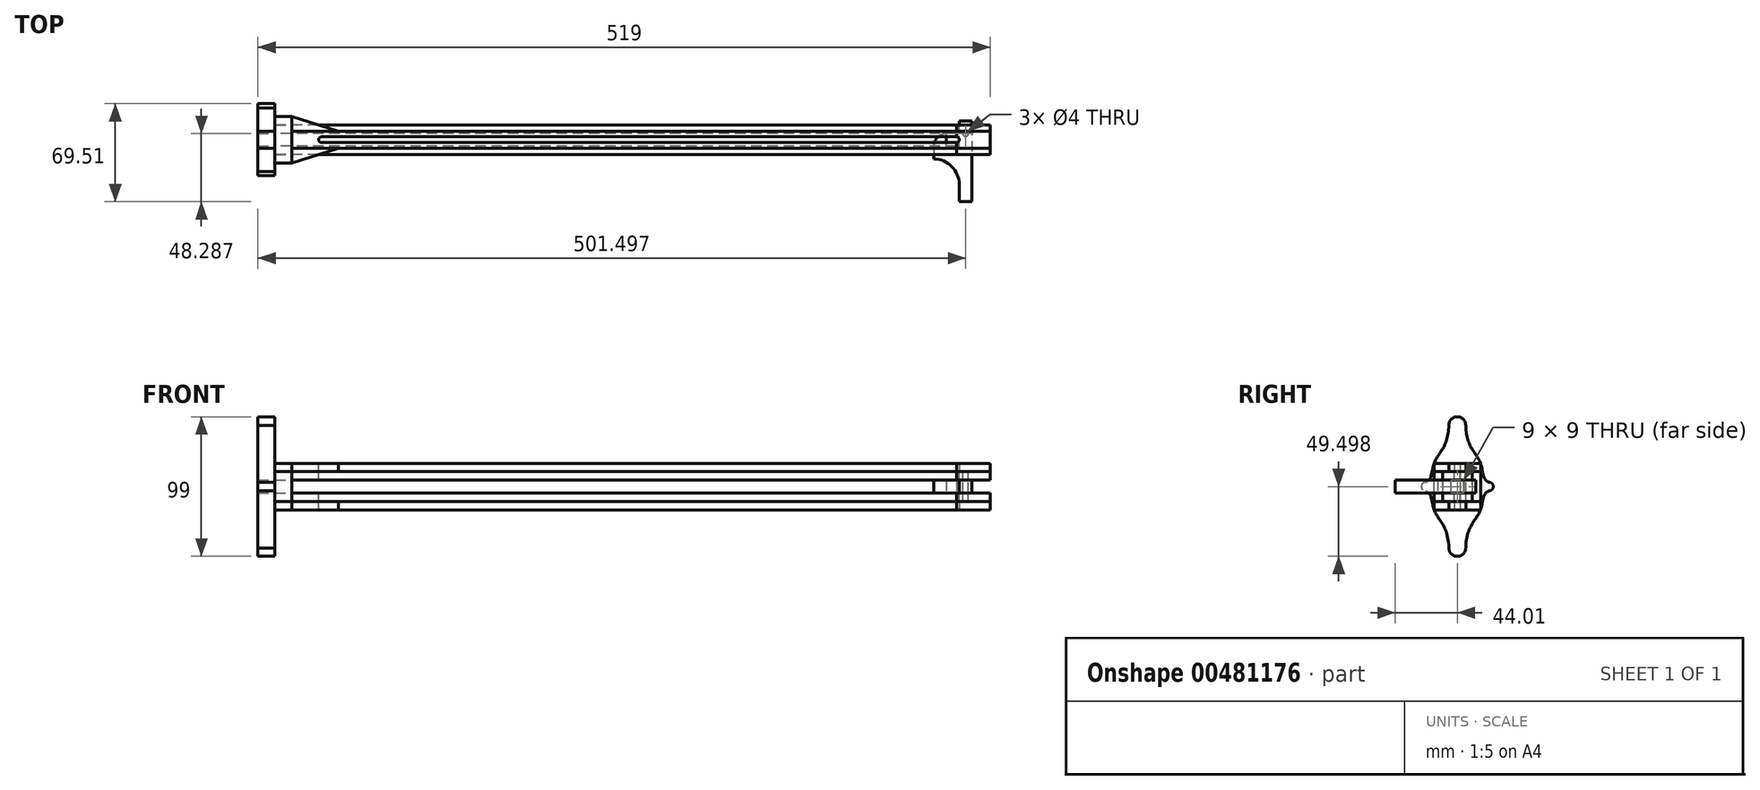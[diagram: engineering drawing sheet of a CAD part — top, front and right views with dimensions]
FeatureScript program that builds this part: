
annotation { "Feature Type Name" : "Feature", "Feature Type Description" : "" }
export const myFeature = defineFeature(function(context is Context, id is Id, definition is map)
    precondition{}
    {
        {
            var Q0;
            Q0=qCreatedBy(makeId("Front.planeOp"),FACE);
            var sketch = newSketch(context, id + "F0", { "sketchPlane" : qUnion([Q0])});
            skLineSegment(sketch, "E0", {"start": v(-257.14, -33.26) * mm, "end": v(225.86, -33.26) * mm});
            skLineSegment(sketch, "E1", {"start": v(-257.14, -42.26) * mm, "end": v(225.86, -42.26) * mm});
            skLineSegment(sketch, "E2", {"start": v(-257.14, -27.26) * mm, "end": v(-257.14, -33.26) * mm});
            skLineSegment(sketch, "E3", {"start": v(-257.14, -27.26) * mm, "end": v(-257.14, -21.26) * mm});
            skLineSegment(sketch, "E4", {"start": v(225.86, -33.26) * mm, "end": v(225.86, -27.26) * mm});
            skLineSegment(sketch, "E5", {"start": v(225.86, -27.26) * mm, "end": v(-257.14, -27.26) * mm});
            skLineSegment(sketch, "E6", {"start": v(225.86, -27.26) * mm, "end": v(225.86, -21.26) * mm});
            skLineSegment(sketch, "E7", {"start": v(225.86, -21.26) * mm, "end": v(-257.14, -21.26) * mm});
            skLineSegment(sketch, "E8", {"start": v(225.86, -42.26) * mm, "end": v(225.86, -48.26) * mm});
            skLineSegment(sketch, "E9", {"start": v(-257.14, -42.26) * mm, "end": v(-257.14, -48.26) * mm});
            skLineSegment(sketch, "E10", {"start": v(-257.14, -48.26) * mm, "end": v(225.86, -48.26) * mm});
            skLineSegment(sketch, "E11", {"start": v(-257.14, -48.26) * mm, "end": v(-257.14, -54.26) * mm});
            skLineSegment(sketch, "E12", {"start": v(225.86, -48.26) * mm, "end": v(225.86, -54.26) * mm});
            skLineSegment(sketch, "E13", {"start": v(225.86, -54.26) * mm, "end": v(-257.14, -54.26) * mm});
            skLineSegment(sketch, "E14", {"start": v(-257.14, -21.26) * mm, "end": v(-245.14, -21.26) * mm});
            skLineSegment(sketch, "E15", {"start": v(-245.14, -21.26) * mm, "end": v(-245.14, -54.26) * mm});
            skLineSegment(sketch, "E16", {"start": v(-245.14, -54.26) * mm, "end": v(-257.14, -54.26) * mm});
            skSolve(sketch);
        }
        {
            var Q0;
            Q0=makeQuery(id+"F0.imprint","IMPRINT",FACE,{"disambiguationData":[TD([[makeQuery(id+"F0.imprint","IMPRINT",EDGE,{"derivedFrom":sQuery(id+"F0.wireOp",EDGE,"E0")}),1.0]])]});
            var Q1;
            Q1=makeQuery(id+"F0.imprint","IMPRINT",FACE,{"disambiguationData":[TD([[makeQuery(id+"F0.imprint","IMPRINT",EDGE,{"derivedFrom":sQuery(id+"F0.wireOp",EDGE,"E1")}),-1.0]])]});
            extrude(context, id + "F1", {"entities" : qUnion([Q0, Q1]), "depth" : 10.5 * mm, "offsetDistance" : 25 * mm, "hasSecondDirection" : true, "secondDirectionOppositeDirection" : true, "secondDirectionDepth" : 10.5 * mm});
        }
        {
            var Q0;
            {var subQ0=sQuery(id+"F0.wireOp",EDGE,"E3");Q0=makeQuery(id+"F0.imprint","IMPRINT",FACE,{"disambiguationData":[TD([[makeQuery(id+"F0.imprint","IMPRINT",EDGE,{"derivedFrom":subQ0}),-1.0]])]});}
            var Q1;
            {var subQ0=sQuery(id+"F0.wireOp",EDGE,"E11");Q1=makeQuery(id+"F0.imprint","IMPRINT",FACE,{"disambiguationData":[TD([[makeQuery(id+"F0.imprint","IMPRINT",EDGE,{"derivedFrom":subQ0}),1.0]])]});}
            extrude(context, id + "F2", {"entities" : qUnion([Q0, Q1]), "depth" : (16.5) * mm, "offsetDistance" : 25 * mm, "hasSecondDirection" : true, "secondDirectionOppositeDirection" : true, "secondDirectionDepth" : 16.5 * mm});
        }
        {
            var Q0;
            {var subQ0=sQuery(id+"F0.wireOp",EDGE,"E12");Q0=makeQuery(id+"F0.imprint","IMPRINT",FACE,{"disambiguationData":[TD([[makeQuery(id+"F0.imprint","IMPRINT",EDGE,{"derivedFrom":subQ0}),-1.0]])]});}
            var Q1;
            {var subQ0=sQuery(id+"F0.wireOp",EDGE,"E6");Q1=makeQuery(id+"F0.imprint","IMPRINT",FACE,{"disambiguationData":[TD([[makeQuery(id+"F0.imprint","IMPRINT",EDGE,{"derivedFrom":subQ0}),1.0]])]});}
            extrude(context, id + "F3", {"entities" : qUnion([Q0, Q1]), "depth" : 6 * mm, "offsetDistance" : 25 * mm, "hasSecondDirection" : true, "secondDirectionOppositeDirection" : true, "secondDirectionDepth" : 6 * mm});
        }
        {
            var Q0;
            Q0=makeQuery(id+"F2.opExtrude","SWEPT_FACE",FACE,{"disambiguationData":[OSD([sQuery(id+"F0.wireOp",EDGE,"E5")])]});
            var sketch = newSketch(context, id + "F4", { "sketchPlane" : qUnion([Q0])});
            skLineSegment(sketch, "E17.bottom", {"start": v(-257.14, 16.5) * mm, "end": v(-245.14, 16.5) * mm});
            skLineSegment(sketch, "E17.top", {"start": v(-257.14, 10.5) * mm, "end": v(-245.14, 10.5) * mm});
            skLineSegment(sketch, "E17.left", {"start": v(-257.14, 16.5) * mm, "end": v(-257.14, 10.5) * mm});
            skLineSegment(sketch, "E17.right", {"start": v(-245.14, 16.5) * mm, "end": v(-245.14, 10.5) * mm});
            skLineSegment(sketch, "E18.bottom", {"start": v(-257.14, -16.5) * mm, "end": v(-245.14, -16.5) * mm});
            skLineSegment(sketch, "E18.top", {"start": v(-257.14, -10.5) * mm, "end": v(-245.14, -10.5) * mm});
            skLineSegment(sketch, "E18.left", {"start": v(-257.14, -16.5) * mm, "end": v(-257.14, -10.5) * mm});
            skLineSegment(sketch, "E18.right", {"start": v(-245.14, -16.5) * mm, "end": v(-245.14, -10.5) * mm});
            skSolve(sketch);
        }
        {
            var Q0;
            Q0 = qSketchRegion(id + "F4", true);
            extrude(context, id + "F5", {"entities" : qUnion([Q0]), "depth" : 21 * mm, "offsetDistance" : 25 * mm});
        }
        {
            var Q0;
            Q0=makeQuery(id+"F1.opExtrude","SWEPT_FACE",FACE,{"disambiguationData":[OSD([sQuery(id+"F0.wireOp",EDGE,"E2")])]});
            var sketch = newSketch(context, id + "F6", { "sketchPlane" : qUnion([Q0])});
            skLineSegment(sketch, "E19.bottom", {"start": v(10.5, -33.26) * mm, "end": v(4.5, -33.26) * mm});
            skLineSegment(sketch, "E19.top", {"start": v(10.5, -42.26) * mm, "end": v(4.5, -42.26) * mm});
            skLineSegment(sketch, "E19.left", {"start": v(10.5, -33.26) * mm, "end": v(10.5, -42.26) * mm});
            skLineSegment(sketch, "E19.right", {"start": v(4.5, -33.26) * mm, "end": v(4.5, -42.26) * mm});
            skLineSegment(sketch, "E20.bottom", {"start": v(-10.5, -33.26) * mm, "end": v(-4.5, -33.26) * mm});
            skLineSegment(sketch, "E20.top", {"start": v(-10.5, -42.26) * mm, "end": v(-4.5, -42.26) * mm});
            skLineSegment(sketch, "E20.left", {"start": v(-10.5, -33.26) * mm, "end": v(-10.5, -42.26) * mm});
            skLineSegment(sketch, "E20.right", {"start": v(-4.5, -33.26) * mm, "end": v(-4.5, -42.26) * mm});
            skSolve(sketch);
        }
        {
            var Q0;
            Q0 = qSketchRegion(id + "F6", true);
            extrude(context, id + "F7", {"entities" : qUnion([Q0]), "oppositeDirection" : true, "depth" : 483 * mm, "offsetDistance" : 25 * mm});
        }
        {
            var Q0;
            Q0=makeQuery(id+"F3.opExtrude","SWEPT_FACE",FACE,{"disambiguationData":[OSD([sQuery(id+"F0.wireOp",EDGE,"E7")])]});
            var sketch = newSketch(context, id + "F8", { "sketchPlane" : qUnion([Q0])});
            skLineSegment(sketch, "E21", {"start": v(-245.14, 6) * mm, "end": v(-245.14, 16.5) * mm});
            skLineSegment(sketch, "E22.MirrorCS", {"start": v(-245.14, -6) * mm, "end": v(-245.14, -16.5) * mm});
            skLineSegment(sketch, "E23", {"start": v(-212.14, -6) * mm, "end": v(-245.14, -16.5) * mm});
            skLineSegment(sketch, "E24", {"start": v(-212.14, 6) * mm, "end": v(-245.14, 16.5) * mm});
            skLineSegment(sketch, "E25", {"start": v(-212.14, -6) * mm, "end": v(-245.14, -6) * mm});
            skLineSegment(sketch, "E26", {"start": v(-245.14, 6) * mm, "end": v(-212.14, 6) * mm});
            skSolve(sketch);
        }
        {
            var Q0;
            Q0=makeQuery(id+"F3.opExtrude","SWEPT_FACE",FACE,{"disambiguationData":[OSD([sQuery(id+"F0.wireOp",EDGE,"E7")])]});
            var sketch = newSketch(context, id + "F9", { "sketchPlane" : qUnion([Q0])});
            skLineSegment(sketch, "E27", {"start": v(225.86, 0) * mm, "end": v(-224.14, 0) * mm});
            skSolve(sketch);
        }
        {
            var Q0;
            Q0 = qSketchRegion(id + "F8", true);
            extrude(context, id + "F10", {"entities" : qUnion([Q0]), "oppositeDirection" : true, "depth" : 6 * mm, "offsetDistance" : 25 * mm});
        }
        {
            var Q0;
            Q0=makeQuery(id+"F1.opExtrude","SWEPT_FACE",FACE,{"disambiguationData":[OSD([sQuery(id+"F0.wireOp",EDGE,"E10")])]});
            var sketch = newSketch(context, id + "F11", { "sketchPlane" : qUnion([Q0])});
            skLineSegment(sketch, "E28", {"start": v(-257.14, -10.5) * mm, "end": v(-245.14, -10.5) * mm});
            skLineSegment(sketch, "E29", {"start": v(-245.14, -10.5) * mm, "end": v(-245.14, -16.5) * mm});
            skLineSegment(sketch, "E30", {"start": v(-245.14, -10.5) * mm, "end": v(-245.14, -6) * mm});
            skLineSegment(sketch, "E31", {"start": v(-245.14, -6) * mm, "end": v(-212.14, -6) * mm});
            skLineSegment(sketch, "E32", {"start": v(-245.14, -16.5) * mm, "end": v(-212.14, -6) * mm});
            skLineSegment(sketch, "E33", {"start": v(-245.14, -6) * mm, "end": v(-245.14, 6) * mm});
            skLineSegment(sketch, "E34", {"start": v(-245.14, 0) * mm, "end": v(-224.95, 0) * mm});
            skLineSegment(sketch, "E35.MirrorCS", {"start": v(-245.14, 10.5) * mm, "end": v(-245.14, 16.5) * mm});
            skLineSegment(sketch, "E36.MirrorCS", {"start": v(-257.14, 10.5) * mm, "end": v(-245.14, 10.5) * mm});
            skLineSegment(sketch, "E37.MirrorCS", {"start": v(-245.14, 16.5) * mm, "end": v(-212.14, 6) * mm});
            skLineSegment(sketch, "E38.MirrorCS", {"start": v(-245.14, 6) * mm, "end": v(-212.14, 6) * mm});
            skLineSegment(sketch, "E39.MirrorCS", {"start": v(-245.14, 6) * mm, "end": v(-245.14, -6) * mm});
            skLineSegment(sketch, "E40.MirrorCS", {"start": v(-245.14, 10.5) * mm, "end": v(-245.14, 6) * mm});
            skSolve(sketch);
        }
        {
            var Q0;
            {var subQ0=sQuery(id+"F11.wireOp",EDGE,"E30");Q0=makeQuery(id+"F11.imprint","IMPRINT",FACE,{"disambiguationData":[TD([[makeQuery(id+"F11.imprint","IMPRINT",EDGE,{"derivedFrom":subQ0}),-1.0]])]});}
            var Q1;
            {var subQ0=sQuery(id+"F11.wireOp",EDGE,"E29");Q1=makeQuery(id+"F11.imprint","IMPRINT",FACE,{"disambiguationData":[TD([[makeQuery(id+"F11.imprint","IMPRINT",EDGE,{"derivedFrom":subQ0}),1.0]])]});}
            var Q2;
            {var subQ0=sQuery(id+"F11.wireOp",EDGE,"E35.MirrorCS");Q2=makeQuery(id+"F11.imprint","IMPRINT",FACE,{"disambiguationData":[TD([[makeQuery(id+"F11.imprint","IMPRINT",EDGE,{"derivedFrom":subQ0}),-1.0]])]});}
            var Q3;
            {var subQ0=sQuery(id+"F11.wireOp",EDGE,"E38.MirrorCS");Q3=makeQuery(id+"F11.imprint","IMPRINT",FACE,{"disambiguationData":[TD([[makeQuery(id+"F11.imprint","IMPRINT",EDGE,{"derivedFrom":subQ0}),1.0]])]});}
            extrude(context, id + "F12", {"entities" : qUnion([Q0, Q1, Q2, Q3]), "depth" : 6 * mm, "offsetDistance" : 25 * mm});
        }
        {
            var Q0;
            Q0=sQuery(id+"F9.wireOp",VERTEX,"E27.end");
            var Q1;
            Q1=sQuery(id+"F9.wireOp",VERTEX,"E27.start");
            var Q2;
            Q2=makeQuery(id+"F1.opExtrude","SWEPT_BODY",BODY,{"disambiguationData":[OSD([sQuery(id+"F0.wireOp",EDGE,"E0"),sQuery(id+"F0.wireOp",EDGE,"E2"),sQuery(id+"F0.wireOp",EDGE,"E4"),sQuery(id+"F0.wireOp",EDGE,"E5")])]});
            var Q3;
            Q3=makeQuery(id+"F1.opExtrude","SWEPT_BODY",BODY,{"disambiguationData":[OSD([sQuery(id+"F0.wireOp",EDGE,"E1"),sQuery(id+"F0.wireOp",EDGE,"E8"),sQuery(id+"F0.wireOp",EDGE,"E9"),sQuery(id+"F0.wireOp",EDGE,"E10")])]});
            var Q4;
            Q4=makeQuery(id+"F3.opExtrude","SWEPT_BODY",BODY,{"disambiguationData":[OSD([sQuery(id+"F0.wireOp",EDGE,"E5"),sQuery(id+"F0.wireOp",EDGE,"E6"),sQuery(id+"F0.wireOp",EDGE,"E7"),sQuery(id+"F0.wireOp",EDGE,"E15")])]});
            var Q5;
            Q5=makeQuery(id+"F3.opExtrude","SWEPT_BODY",BODY,{"disambiguationData":[OSD([sQuery(id+"F0.wireOp",EDGE,"E10"),sQuery(id+"F0.wireOp",EDGE,"E12"),sQuery(id+"F0.wireOp",EDGE,"E13"),sQuery(id+"F0.wireOp",EDGE,"E15")])]});
            hole(context, id + "F13", {"style" : HoleStyle.SIMPLE, "endStyle" : HoleEndStyle.THROUGH, "holeDiameter" : 4 * mm, "majorDiameter" : 5 * mm, "isTappedThrough" : true, "tappedDepth" : 12 * mm, "tapClearance" : 3, "locations" : qUnion([Q0, Q1]), "scope" : qUnion([Q2, Q3, Q4, Q5])});
        }
        {
            var Q0;
            Q0=makeQuery(id+"F3.opExtrude","SWEPT_FACE",FACE,{"disambiguationData":[OSD([sQuery(id+"F0.wireOp",EDGE,"E7")])]});
            var sketch = newSketch(context, id + "F14", { "sketchPlane" : qUnion([Q0])});
            skLineSegment(sketch, "E41.bottom", {"start": v(225.86, 2) * mm, "end": v(-224.14, 2) * mm});
            skLineSegment(sketch, "E41.top", {"start": v(225.86, -2) * mm, "end": v(-224.14, -2) * mm});
            skLineSegment(sketch, "E41.left", {"start": v(225.86, 2) * mm, "end": v(225.86, -2) * mm});
            skLineSegment(sketch, "E41.right", {"start": v(-224.14, 2) * mm, "end": v(-224.14, -2) * mm});
            skSolve(sketch);
        }
        {
            var Q0;
            Q0 = qSketchRegion(id + "F14", true);
            extrude(context, id + "F15", {"entities" : qUnion([Q0]), "operationType" : NewBodyOperationType.REMOVE, "oppositeDirection" : true, "depth" : 45 * mm, "offsetDistance" : 25 * mm});
        }
        {
            var Q0;
            {var subQ0=sQuery(id+"F0.wireOp",EDGE,"E5");var subQ1=sQuery(id+"F0.wireOp",EDGE,"E7");var subQ2=sQuery(id+"F0.wireOp",EDGE,"E6");Q0=makeQuery(id+"F13.hole-1.boolean.opBoolean","SPLIT",FACE,{"disambiguationData":[TD([makeQuery(id+"F3.opExtrude","CAP_FACE",FACE,{"disambiguationData":[OSD([subQ0,subQ2,subQ1,sQuery(id+"F0.wireOp",EDGE,"E15")])],"isStart":true})])],"derivedFrom":makeQuery(id+"F3.opExtrude","SWEPT_FACE",FACE,{"disambiguationData":[OSD([subQ2])]})});}
            var sketch = newSketch(context, id + "F16", { "sketchPlane" : qUnion([Q0])});
            skLineSegment(sketch, "E42", {"start": v(6, -21.26) * mm, "end": v(-6, -21.26) * mm});
            skLineSegment(sketch, "E43", {"start": v(6, -27.26) * mm, "end": v(-6, -27.26) * mm});
            skLineSegment(sketch, "E44", {"start": v(6, -21.26) * mm, "end": v(6, -27.26) * mm});
            skLineSegment(sketch, "E45", {"start": v(-6, -21.26) * mm, "end": v(-6, -27.26) * mm});
            skLineSegment(sketch, "E46", {"start": v(6, -54.26) * mm, "end": v(-6, -54.26) * mm});
            skLineSegment(sketch, "E47", {"start": v(-6, -54.26) * mm, "end": v(-6, -48.26) * mm});
            skLineSegment(sketch, "E48", {"start": v(-6, -48.26) * mm, "end": v(6, -48.26) * mm});
            skLineSegment(sketch, "E49", {"start": v(6, -48.26) * mm, "end": v(6, -54.26) * mm});
            skSolve(sketch);
        }
        {
            var Q0;
            Q0 = qSketchRegion(id + "F16", true);
            extrude(context, id + "F17", {"entities" : qUnion([Q0]), "depth" : 24 * mm, "offsetDistance" : 25 * mm});
        }
        {
            var Q0;
            Q0=makeQuery(id+"F1.opExtrude","SWEPT_FACE",FACE,{"disambiguationData":[OSD([sQuery(id+"F0.wireOp",EDGE,"E9")])]});
            var sketch = newSketch(context, id + "F18", { "sketchPlane" : qUnion([Q0])});
            skLineSegment(sketch, "E50", {"start": v(0, -54.26) * mm, "end": v(0, -87.26) * mm});
            skLineSegment(sketch, "E51", {"start": v(0, -21.26) * mm, "end": v(0, 11.74) * mm});
            skLineSegment(sketch, "E52", {"start": v(-16.5, -37.76) * mm, "end": v(-22.5, -37.76) * mm});
            skLineSegment(sketch, "E53", {"start": v(16.5, -37.76) * mm, "end": v(22.5, -37.76) * mm});
            skCircle(sketch, "E54", {"center": v(-22.5, -37.76) * mm, "radius": 3 * mm});
            skLineSegment(sketch, "E55", {"start": v(16.5, -37.76) * mm, "end": v(19.5, -37.76) * mm});
            skCircle(sketch, "E56", {"center": v(22.5, -37.76) * mm, "radius": 3 * mm});
            skLineSegment(sketch, "E57", {"start": v(-16.5, -37.76) * mm, "end": v(-16.5, -27.26) * mm});
            skLineSegment(sketch, "E58", {"start": v(16.5, -37.76) * mm, "end": v(16.5, -48.26) * mm});
            skLineSegment(sketch, "E59", {"start": v(16.5, -37.76) * mm, "end": v(16.5, -27.26) * mm});
            skLineSegment(sketch, "E60", {"start": v(0, -87.26) * mm, "end": v(0, -84.26) * mm});
            skLineSegment(sketch, "E61", {"start": v(0, 11.74) * mm, "end": v(0, 8.74) * mm});
            skLineSegment(sketch, "E62", {"start": v(0, -87.26) * mm, "end": v(0, -81.26) * mm});
            skCircle(sketch, "E63", {"center": v(0, -81.26) * mm, "radius": 6 * mm});
            skLineSegment(sketch, "E64", {"start": v(0, -21.26) * mm, "end": v(0, 5.74) * mm});
            skCircle(sketch, "E65", {"center": v(0, 5.74) * mm, "radius": 6 * mm});
            skLineSegment(sketch, "E66.bottom", {"start": v(-16.5, -54.26) * mm, "end": v(16.5, -54.26) * mm});
            skLineSegment(sketch, "E66.top", {"start": v(-16.5, -21.26) * mm, "end": v(16.5, -21.26) * mm});
            skLineSegment(sketch, "E66.left", {"start": v(-16.5, -54.26) * mm, "end": v(-16.5, -21.26) * mm});
            skLineSegment(sketch, "E66.right", {"start": v(16.5, -54.26) * mm, "end": v(16.5, -21.26) * mm});
            skLineSegment(sketch, "E67", {"start": v(-4.5, -37.76) * mm, "end": v(-4.5, -33.26) * mm});
            skLineSegment(sketch, "E68", {"start": v(4.5, -37.76) * mm, "end": v(4.5, -42.26) * mm});
            skLineSegment(sketch, "E69.bottom", {"start": v(4.5, -42.26) * mm, "end": v(-4.5, -42.26) * mm});
            skLineSegment(sketch, "E69.top", {"start": v(4.5, -33.26) * mm, "end": v(-4.5, -33.26) * mm});
            skLineSegment(sketch, "E69.left", {"start": v(4.5, -42.26) * mm, "end": v(4.5, -33.26) * mm});
            skLineSegment(sketch, "E69.right", {"start": v(-4.5, -42.26) * mm, "end": v(-4.5, -33.26) * mm});
            skFitSpline(sketch, "E70", {"points": [v(-22.5, -40.76) * mm, v(-16.5, -54.26) * mm, v(-6, -81.26) * mm], "startDerivative": vector(34.79, -10.64) * mm, "endDerivative": vector(1.67, -81.78) * mm});
            skFitSpline(sketch, "E71.MirrorCS", {"points": [v(-22.5, -34.76) * mm, v(-16.5, -21.26) * mm, v(-6, 5.74) * mm], "startDerivative": vector(34.79, 10.64) * mm, "endDerivative": vector(1.67, 81.78) * mm});
            skFitSpline(sketch, "E72.MirrorCS", {"points": [v(22.5, -34.76) * mm, v(16.5, -21.26) * mm, v(6, 5.74) * mm], "startDerivative": vector(-34.79, 10.64) * mm, "endDerivative": vector(-1.67, 81.78) * mm});
            skFitSpline(sketch, "E73.MirrorCS", {"points": [v(22.5, -40.76) * mm, v(16.5, -54.26) * mm, v(6, -81.26) * mm], "startDerivative": vector(-34.79, -10.64) * mm, "endDerivative": vector(-1.67, -81.78) * mm});
            skLineSegment(sketch, "E74", {"start": v(0, -0.26) * mm, "end": v(6.53, -0.26) * mm});
            skLineSegment(sketch, "E75", {"start": v(6.53, -0.26) * mm, "end": v(-6.53, -0.26) * mm});
            skSolve(sketch);
        }
        {
            var Q0;
            Q0 = qSketchRegion(id + "F18", true);
            extrude(context, id + "F19", {"entities" : qUnion([Q0]), "depth" : 12 * mm, "offsetDistance" : 25 * mm});
        }
        {
            var Q0;
            Q0=makeQuery(id+"F17.opExtrude","SWEPT_FACE",FACE,{"disambiguationData":[OSD([sQuery(id+"F16.wireOp",EDGE,"E46")])]});
            var sketch = newSketch(context, id + "F20", { "sketchPlane" : qUnion([Q0])});
            skLineSegment(sketch, "E76", {"start": v(225.86, 6) * mm, "end": v(225.86, -6) * mm});
            skCircle(sketch, "E77", {"center": v(225.86, 0) * mm, "radius": 2 * mm});
            skSolve(sketch);
        }
        {
            var Q0;
            {var subQ0=sQuery(id+"F20.wireOp",EDGE,"E77");var subQ1=sQuery(id+"F20.wireOp",EDGE,"E76");var subQ2=makeQuery(id+"F20.imprint","INTERSECT",VERTEX,{"disambiguationData":[OD(0.0)],"derivedFrom":[subQ1,subQ0]});Q0=makeQuery(id+"F20.imprint","IMPRINT",FACE,{"disambiguationData":[TD([[makeQuery(id+"F20.imprint","IMPRINT",EDGE,{"disambiguationData":[TD([[subQ2,-1.0]])],"derivedFrom":subQ1}),-1.0]])]});}
            var Q1;
            {var subQ0=sQuery(id+"F20.wireOp",EDGE,"E77");var subQ1=sQuery(id+"F20.wireOp",EDGE,"E76");var subQ2=makeQuery(id+"F20.imprint","INTERSECT",VERTEX,{"disambiguationData":[OD(0.0)],"derivedFrom":[subQ1,subQ0]});Q1=makeQuery(id+"F20.imprint","IMPRINT",FACE,{"disambiguationData":[TD([[makeQuery(id+"F20.imprint","IMPRINT",EDGE,{"disambiguationData":[TD([[subQ2,-1.0]])],"derivedFrom":subQ1}),1.0]])]});}
            extrude(context, id + "F21", {"entities" : qUnion([Q0, Q1]), "operationType" : NewBodyOperationType.REMOVE, "oppositeDirection" : true, "depth" : 46.3 * mm, "offsetDistance" : 25 * mm});
        }
        {
            var Q0;
            {var subQ0=sQuery(id+"F0.wireOp",EDGE,"E0");var subQ1=sQuery(id+"F0.wireOp",EDGE,"E5");var subQ2=sQuery(id+"F0.wireOp",EDGE,"E4");Q0=makeQuery(id+"F13.hole-1.boolean.opBoolean","SPLIT",FACE,{"disambiguationData":[TD([makeQuery(id+"F1.opExtrude","CAP_FACE",FACE,{"disambiguationData":[OSD([subQ0,sQuery(id+"F0.wireOp",EDGE,"E2"),subQ2,subQ1])],"isStart":true})])],"derivedFrom":makeQuery(id+"F1.opExtrude","SWEPT_FACE",FACE,{"disambiguationData":[OSD([subQ2])]})});}
            var sketch = newSketch(context, id + "F22", { "sketchPlane" : qUnion([Q0])});
            skLineSegment(sketch, "E78.bottom", {"start": v(10.5, -27.26) * mm, "end": v(2, -27.26) * mm});
            skLineSegment(sketch, "E78.top", {"start": v(10.5, -33.26) * mm, "end": v(2, -33.26) * mm});
            skLineSegment(sketch, "E79.bottom", {"start": v(10.5, -27.26) * mm, "end": v(-10.5, -27.26) * mm});
            skLineSegment(sketch, "E79.top", {"start": v(10.5, -33.26) * mm, "end": v(-10.5, -33.26) * mm});
            skLineSegment(sketch, "E79.left", {"start": v(10.5, -27.26) * mm, "end": v(10.5, -33.26) * mm});
            skLineSegment(sketch, "E79.right", {"start": v(-10.5, -27.26) * mm, "end": v(-10.5, -33.26) * mm});
            skLineSegment(sketch, "E80", {"start": v(10.5, -33.26) * mm, "end": v(10.5, -42.26) * mm});
            skLineSegment(sketch, "E81.bottom", {"start": v(10.5, -42.26) * mm, "end": v(-10.5, -42.26) * mm});
            skLineSegment(sketch, "E81.top", {"start": v(10.5, -48.26) * mm, "end": v(-10.5, -48.26) * mm});
            skLineSegment(sketch, "E81.left", {"start": v(10.5, -42.26) * mm, "end": v(10.5, -48.26) * mm});
            skLineSegment(sketch, "E81.right", {"start": v(-10.5, -42.26) * mm, "end": v(-10.5, -48.26) * mm});
            skLineSegment(sketch, "E82", {"start": v(-10.5, -33.26) * mm, "end": v(-10.5, -42.26) * mm});
            skSolve(sketch);
        }
        {
            var Q0;
            {var subQ0=sQuery(id+"F22.wireOp",EDGE,"E79.left");Q0=makeQuery(id+"F22.imprint","IMPRINT",FACE,{"disambiguationData":[TD([[makeQuery(id+"F22.imprint","IMPRINT",EDGE,{"derivedFrom":subQ0}),1.0]])]});}
            var Q1;
            {var subQ3=sQuery(id+"F22.wireOp",EDGE,"E79.right");Q1=makeQuery(id+"F22.imprint","IMPRINT",FACE,{"disambiguationData":[TD([[makeQuery(id+"F22.imprint","IMPRINT",EDGE,{"derivedFrom":subQ3}),1.0]])]});}
            var Q2;
            Q2=makeQuery(id+"F22.imprint","IMPRINT",FACE,{"disambiguationData":[TD([[makeQuery(id+"F22.imprint","IMPRINT",EDGE,{"derivedFrom":sQuery(id+"F22.wireOp",EDGE,"E81.bottom")}),1.0]])]});
            extrude(context, id + "F23", {"entities" : qUnion([Q0, Q1, Q2]), "depth" : 24 * mm, "offsetDistance" : 25 * mm});
        }
        {
            var Q0;
            Q0=makeQuery(id+"F23.opExtrude","SWEPT_FACE",FACE,{"disambiguationData":[OSD([sQuery(id+"F22.wireOp",EDGE,"E79.bottom")])]});
            var sketch = newSketch(context, id + "F24", { "sketchPlane" : qUnion([Q0])});
            skCircle(sketch, "E83", {"center": v(225.86, 0) * mm, "radius": 2 * mm});
            skSolve(sketch);
        }
        {
            var Q0;
            {var subQ0=sQuery(id+"F24.wireOp",EDGE,"E83");var subQ1=makeQuery(id+"F23.opExtrude","CAP_EDGE",EDGE,{"disambiguationData":[OSD([sQuery(id+"F22.wireOp",EDGE,"E79.bottom")])],"isStart":true});var subQ2=makeQuery(id+"F24.imprint","INTERSECT",VERTEX,{"disambiguationData":[OD(0.0)],"derivedFrom":[subQ1,subQ0]});Q0=makeQuery(id+"F24.imprint","IMPRINT",FACE,{"disambiguationData":[TD([[makeQuery(id+"F24.imprint","IMPRINT",EDGE,{"disambiguationData":[TD([[subQ2,1.0]])],"derivedFrom":subQ0}),1.0]])]});}
            extrude(context, id + "F25", {"entities" : qUnion([Q0]), "operationType" : NewBodyOperationType.REMOVE, "oppositeDirection" : true, "depth" : 47.8 * mm, "offsetDistance" : 25 * mm});
        }
        {
            var Q0;
            Q0=makeQuery(id+"F3.opExtrude","SWEPT_FACE",FACE,{"disambiguationData":[OSD([sQuery(id+"F0.wireOp",EDGE,"E7")])]});
            var sketch = newSketch(context, id + "F26", { "sketchPlane" : qUnion([Q0])});
            skLineSegment(sketch, "E84", {"start": v(225.86, -0.22) * mm, "end": v(227.86, -0.22) * mm});
            skLineSegment(sketch, "E85", {"start": v(227.86, -0.22) * mm, "end": v(227.86, -4.72) * mm});
            skLineSegment(sketch, "E86", {"start": v(227.86, -0.22) * mm, "end": v(227.86, 4.28) * mm});
            skLineSegment(sketch, "E87", {"start": v(227.86, -4.72) * mm, "end": v(218.86, -4.72) * mm});
            skLineSegment(sketch, "E88", {"start": v(218.86, -4.72) * mm, "end": v(209.86, -4.72) * mm});
            skLineSegment(sketch, "E89", {"start": v(218.86, -4.72) * mm, "end": v(218.86, 4.28) * mm});
            skArc(sketch, "E90", {"start": v(209.86, -4.72) * mm, "mid": v(212.5, 1.64) * mm, "end": v(218.86, 4.28) * mm});
            skLineSegment(sketch, "E91", {"start": v(236.86, 8.78) * mm, "end": v(236.86, -4.72) * mm});
            skLineSegment(sketch, "E92", {"start": v(236.86, -4.72) * mm, "end": v(236.86, -22.72) * mm});
            skLineSegment(sketch, "E93", {"start": v(227.86, 4.28) * mm, "end": v(236.86, 4.28) * mm});
            skCircle(sketch, "E94", {"center": v(232.36, 4.28) * mm, "radius": 0.94 * mm});
            skLineSegment(sketch, "E95", {"start": v(227.86, -44) * mm, "end": v(236.86, -44) * mm});
            skLineSegment(sketch, "E96", {"start": v(236.86, -44) * mm, "end": v(236.86, -22.72) * mm});
            skLineSegment(sketch, "E97", {"start": v(236.86, 4.28) * mm, "end": v(236.86, 13.28) * mm});
            skLineSegment(sketch, "E98", {"start": v(227.86, 4.28) * mm, "end": v(227.86, 13.28) * mm});
            skLineSegment(sketch, "E99", {"start": v(227.86, 13.28) * mm, "end": v(236.86, 13.28) * mm});
            skLineSegment(sketch, "E100", {"start": v(209.86, -4.72) * mm, "end": v(209.86, -13.72) * mm});
            skLineSegment(sketch, "E101", {"start": v(227.86, -4.72) * mm, "end": v(227.86, -31.72) * mm});
            skLineSegment(sketch, "E102", {"start": v(209.86, -13.72) * mm, "end": v(227.86, -13.72) * mm});
            skArc(sketch, "E103", {"start": v(209.86, -13.72) * mm, "mid": v(222.58, -19) * mm, "end": v(227.86, -31.72) * mm});
            skLineSegment(sketch, "E104", {"start": v(227.86, -31.72) * mm, "end": v(227.86, -44) * mm});
            skSolve(sketch);
        }
        {
            var Q0;
            Q0 = qSketchRegion(id + "F26", true);
            extrude(context, id + "F27", {"entities" : qUnion([Q0]), "depth" : 9 * mm, "offsetDistance" : 25 * mm});
        }
        {
            var Q0;
            Q0=makeQuery(id+"F27.opExtrude","SWEPT_BODY",BODY,{"disambiguationData":[OSD([sQuery(id+"F26.wireOp",EDGE,"E85"),sQuery(id+"F26.wireOp",EDGE,"E86"),sQuery(id+"F26.wireOp",EDGE,"E87"),sQuery(id+"F26.wireOp",EDGE,"E89"),sQuery(id+"F26.wireOp",EDGE,"E90"),sQuery(id+"F26.wireOp",EDGE,"E91"),sQuery(id+"F26.wireOp",EDGE,"E92"),sQuery(id+"F26.wireOp",EDGE,"E94"),sQuery(id+"F26.wireOp",EDGE,"E95"),sQuery(id+"F26.wireOp",EDGE,"E96"),sQuery(id+"F26.wireOp",EDGE,"E97"),sQuery(id+"F26.wireOp",EDGE,"E98"),sQuery(id+"F26.wireOp",EDGE,"E99"),sQuery(id+"F26.wireOp",EDGE,"E100"),sQuery(id+"F26.wireOp",EDGE,"E103"),sQuery(id+"F26.wireOp",EDGE,"E104")])]});
            var Q1;
            Q1=makeQuery(id+"F27.opExtrude","CAP_FACE",FACE,{"disambiguationData":[OSD([sQuery(id+"F26.wireOp",EDGE,"E85"),sQuery(id+"F26.wireOp",EDGE,"E86"),sQuery(id+"F26.wireOp",EDGE,"E87"),sQuery(id+"F26.wireOp",EDGE,"E89"),sQuery(id+"F26.wireOp",EDGE,"E90"),sQuery(id+"F26.wireOp",EDGE,"E91"),sQuery(id+"F26.wireOp",EDGE,"E92"),sQuery(id+"F26.wireOp",EDGE,"E94"),sQuery(id+"F26.wireOp",EDGE,"E95"),sQuery(id+"F26.wireOp",EDGE,"E96"),sQuery(id+"F26.wireOp",EDGE,"E97"),sQuery(id+"F26.wireOp",EDGE,"E98"),sQuery(id+"F26.wireOp",EDGE,"E99"),sQuery(id+"F26.wireOp",EDGE,"E100"),sQuery(id+"F26.wireOp",EDGE,"E103"),sQuery(id+"F26.wireOp",EDGE,"E104")])],"isStart":false});
            var Q2;
            Q2=makeQuery(id+"F27.opExtrude","SWEPT_EDGE",EDGE,{"disambiguationData":[OSD([sQuery(id+"F26.wireOp",EDGE,"E95"),sQuery(id+"F26.wireOp",EDGE,"E96")])]});
            transform(context, id + "F28", {"entities" : qUnion([Q0]), "transformType" : TransformType.TRANSLATION_DISTANCE, "transformDirection" : qUnion([Q1, Q2]), "distance" : 21 * mm, "makeCopy" : false});
        }
        {
            var Q0;
            Q0=makeQuery(id+"F27.opExtrude","CAP_FACE",FACE,{"disambiguationData":[OSD([sQuery(id+"F26.wireOp",EDGE,"E85"),sQuery(id+"F26.wireOp",EDGE,"E86"),sQuery(id+"F26.wireOp",EDGE,"E87"),sQuery(id+"F26.wireOp",EDGE,"E89"),sQuery(id+"F26.wireOp",EDGE,"E90"),sQuery(id+"F26.wireOp",EDGE,"E91"),sQuery(id+"F26.wireOp",EDGE,"E92"),sQuery(id+"F26.wireOp",EDGE,"E94"),sQuery(id+"F26.wireOp",EDGE,"E95"),sQuery(id+"F26.wireOp",EDGE,"E96"),sQuery(id+"F26.wireOp",EDGE,"E97"),sQuery(id+"F26.wireOp",EDGE,"E98"),sQuery(id+"F26.wireOp",EDGE,"E99"),sQuery(id+"F26.wireOp",EDGE,"E100"),sQuery(id+"F26.wireOp",EDGE,"E103"),sQuery(id+"F26.wireOp",EDGE,"E104")])],"isStart":false});
            var sketch = newSketch(context, id + "F29", { "sketchPlane" : qUnion([Q0])});
            skCircle(sketch, "E105", {"center": v(232.36, 4.28) * mm, "radius": 2 * mm});
            skSolve(sketch);
        }
        {
            var Q0;
            Q0 = qSketchRegion(id + "F29", true);
            extrude(context, id + "F30", {"entities" : qUnion([Q0]), "operationType" : NewBodyOperationType.REMOVE, "oppositeDirection" : true, "depth" : 15 * mm, "offsetDistance" : 25 * mm, "hasSecondDirection" : true, "secondDirectionOppositeDirection" : false, "secondDirectionDepth" : 6 * mm});
        }
    });
